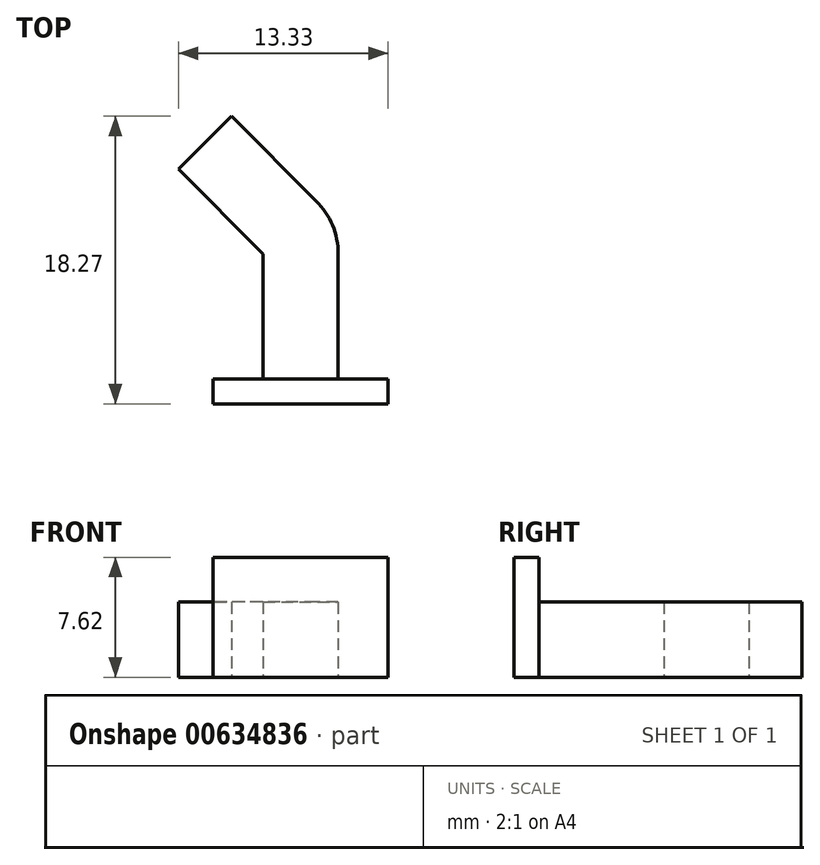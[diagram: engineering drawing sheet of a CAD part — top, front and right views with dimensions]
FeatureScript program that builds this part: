
annotation { "Feature Type Name" : "Feature", "Feature Type Description" : "" }
export const myFeature = defineFeature(function(context is Context, id is Id, definition is map)
    precondition{}
    {
        {
            var Q0;
            Q0=qCreatedBy(makeId("Top.planeOp"),FACE);
            var sketch = newSketch(context, id + "F0", { "sketchPlane" : qUnion([Q0])});
            skLineSegment(sketch, "E0.bottom", {"start": v(-4.76, -18.39) * mm, "end": v(0, -18.39) * mm});
            skLineSegment(sketch, "E0.top", {"start": v(-4.76, -10.45) * mm, "end": v(0, -10.45) * mm});
            skLineSegment(sketch, "E0.left", {"start": v(-4.76, -18.39) * mm, "end": v(-4.76, -10.45) * mm});
            skLineSegment(sketch, "E0.right", {"start": v(0, -18.39) * mm, "end": v(0, -10.45) * mm});
            skLineSegment(sketch, "E1", {"start": v(-4.76, -10.45) * mm, "end": v(-4.76, -5.07) * mm, "construction": true});
            skLineSegment(sketch, "E2", {"start": v(-4.76, -10.45) * mm, "end": v(-10.15, -5.07) * mm});
            skLineSegment(sketch, "E3", {"start": v(-10.15, -5.07) * mm, "end": v(-6.78, -1.7) * mm});
            skLineSegment(sketch, "E4", {"start": v(-4.76, -10.45) * mm, "end": v(-1.4, -7.08) * mm});
            skLineSegment(sketch, "E5", {"start": v(-1.4, -7.08) * mm, "end": v(-6.78, -1.7) * mm});
            skArc(sketch, "E6", {"start": v(-1.4, -7.08) * mm, "mid": v(-0.36, -8.63) * mm, "end": v(0, -10.45) * mm});
            skLineSegment(sketch, "E7.bottom", {"start": v(-7.94, -18.39) * mm, "end": v(3.18, -18.39) * mm});
            skLineSegment(sketch, "E7.top", {"start": v(-7.94, -19.97) * mm, "end": v(3.18, -19.97) * mm});
            skLineSegment(sketch, "E7.left", {"start": v(-7.94, -18.39) * mm, "end": v(-7.94, -19.97) * mm});
            skLineSegment(sketch, "E7.right", {"start": v(3.18, -18.39) * mm, "end": v(3.18, -19.97) * mm});
            skLineSegment(sketch, "E8.bottom", {"start": v(11.01, 3.3) * mm, "end": v(49.11, 3.3) * mm});
            skLineSegment(sketch, "E8.top", {"start": v(11.01, -22.1) * mm, "end": v(49.11, -22.1) * mm});
            skLineSegment(sketch, "E8.left", {"start": v(11.01, 3.3) * mm, "end": v(11.01, -22.1) * mm});
            skLineSegment(sketch, "E8.right", {"start": v(49.11, 3.3) * mm, "end": v(49.11, -22.1) * mm});
            skLineSegment(sketch, "E9.bottom", {"start": v(27.52, -6.86) * mm, "end": v(32.6, -6.86) * mm});
            skLineSegment(sketch, "E9.top", {"start": v(27.52, -11.94) * mm, "end": v(32.6, -11.94) * mm});
            skLineSegment(sketch, "E9.left", {"start": v(27.52, -6.86) * mm, "end": v(27.52, -11.94) * mm});
            skLineSegment(sketch, "E9.right", {"start": v(32.6, -6.86) * mm, "end": v(32.6, -11.94) * mm});
            skLineSegment(sketch, "E10", {"start": v(11.01, 3.3) * mm, "end": v(30.06, 3.3) * mm});
            skLineSegment(sketch, "E11", {"start": v(30.06, 3.3) * mm, "end": v(30.06, -6.86) * mm});
            skLineSegment(sketch, "E12", {"start": v(27.52, -6.86) * mm, "end": v(30.06, -6.86) * mm});
            skSolve(sketch);
        }
        {
            var Q0;
            Q0=makeQuery(id+"F0.imprint","IMPRINT",FACE,{"disambiguationData":[TD([[makeQuery(id+"F0.imprint","IMPRINT",EDGE,{"derivedFrom":sQuery(id+"F0.wireOp",EDGE,"E7.top")}),1.0]])]});
            extrude(context, id + "F1", {"entities" : qUnion([Q0]), "depth" : 7.62 * mm, "offsetDistance" : 25.4 * mm});
        }
        {
            var Q0;
            Q0=makeQuery(id+"F0.imprint","IMPRINT",FACE,{"disambiguationData":[TD([[makeQuery(id+"F0.imprint","IMPRINT",EDGE,{"derivedFrom":sQuery(id+"F0.wireOp",EDGE,"E0.top")}),-1.0]])]});
            var Q1;
            Q1=makeQuery(id+"F0.imprint","IMPRINT",FACE,{"disambiguationData":[TD([[makeQuery(id+"F0.imprint","IMPRINT",EDGE,{"derivedFrom":sQuery(id+"F0.wireOp",EDGE,"E0.top")}),1.0]])]});
            var Q2;
            Q2=makeQuery(id+"F0.imprint","IMPRINT",FACE,{"disambiguationData":[TD([[makeQuery(id+"F0.imprint","IMPRINT",EDGE,{"derivedFrom":sQuery(id+"F0.wireOp",EDGE,"E2")}),-1.0]])]});
            extrude(context, id + "F2", {"entities" : qUnion([Q0, Q1, Q2]), "operationType" : NewBodyOperationType.ADD, "depth" : 4.78 * mm, "offsetDistance" : 25.4 * mm});
        }
        {
            var Q0;
            Q0=makeQuery(id+"F0.imprint","IMPRINT",FACE,{"disambiguationData":[TD([[makeQuery(id+"F0.imprint","IMPRINT",EDGE,{"derivedFrom":sQuery(id+"F0.wireOp",EDGE,"E8.bottom")}),-1.0]])]});
            extrude(context, id + "F3", {"entities" : qUnion([Q0]), "depth" : 3.17 * mm, "offsetDistance" : 25.4 * mm});
        }
        {
            var Q0;
            Q0=makeQuery(id+"F3.opExtrude","SWEPT_BODY",BODY,{"disambiguationData":[OSD([sQuery(id+"F0.wireOp",EDGE,"E8.bottom"),sQuery(id+"F0.wireOp",EDGE,"E8.top"),sQuery(id+"F0.wireOp",EDGE,"E8.left"),sQuery(id+"F0.wireOp",EDGE,"E8.right"),sQuery(id+"F0.wireOp",EDGE,"E9.bottom"),sQuery(id+"F0.wireOp",EDGE,"E9.top"),sQuery(id+"F0.wireOp",EDGE,"E9.left"),sQuery(id+"F0.wireOp",EDGE,"E9.right"),sQuery(id+"F0.wireOp",EDGE,"E10"),sQuery(id+"F0.wireOp",EDGE,"E12")])]});
            deleteBodies(context, id + "F4", {"entities" : qUnion([Q0])});
        }
    });
